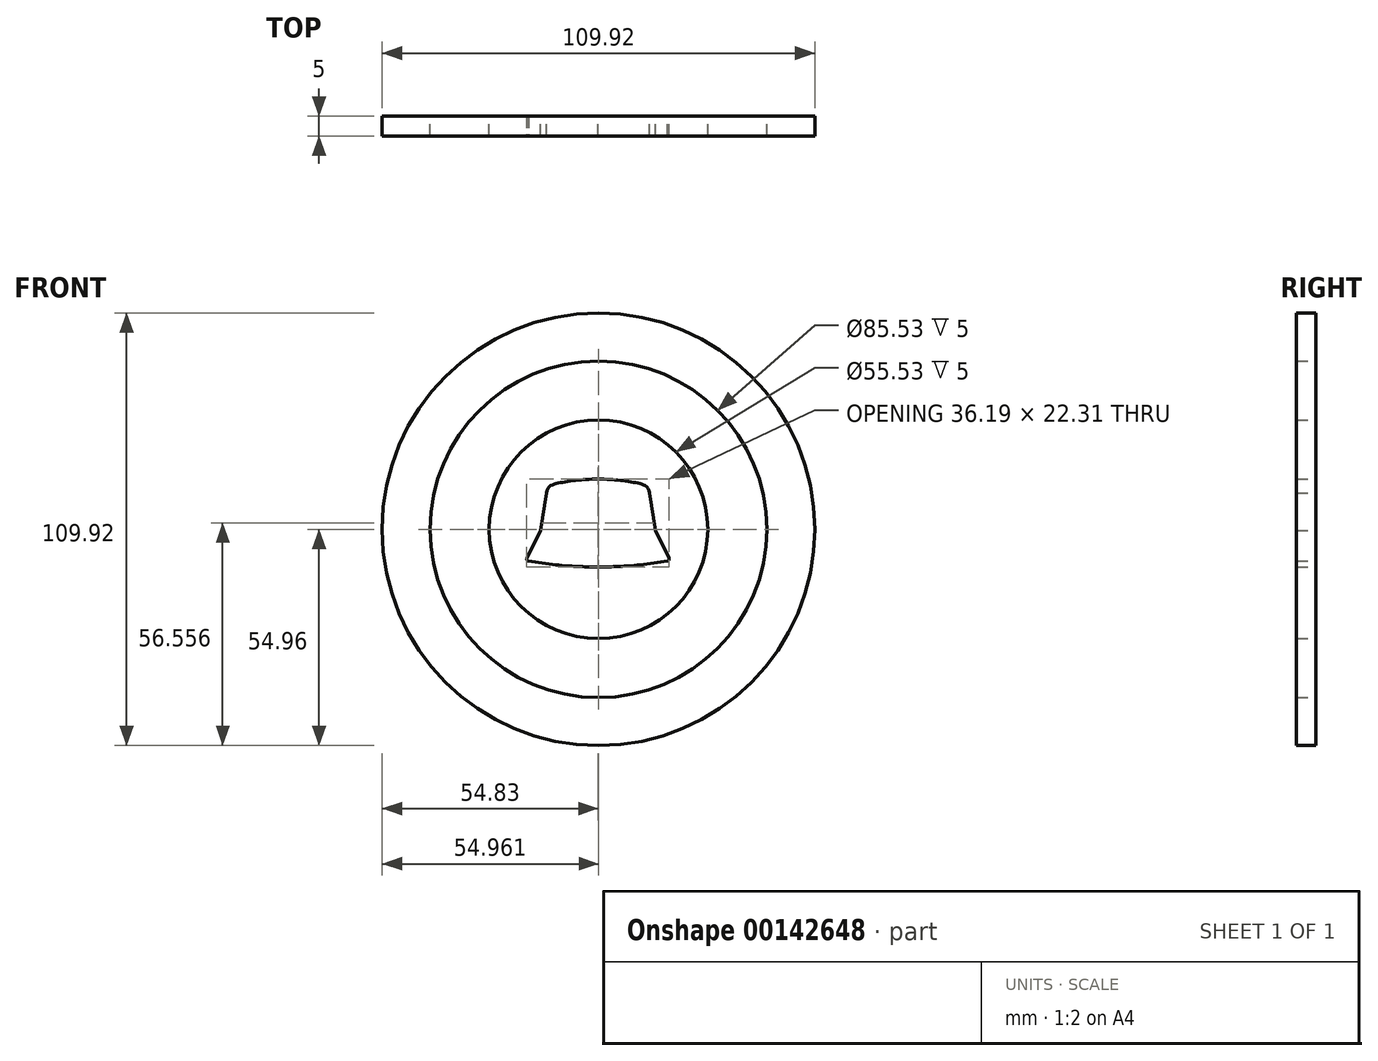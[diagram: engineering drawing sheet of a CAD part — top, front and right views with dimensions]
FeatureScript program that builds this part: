
annotation { "Feature Type Name" : "Feature", "Feature Type Description" : "" }
export const myFeature = defineFeature(function(context is Context, id is Id, definition is map)
    precondition{}
    {
        {
            var Q0;
            Q0=qCreatedBy(makeId("Front.planeOp"),FACE);
            var sketch = newSketch(context, id + "F0", { "sketchPlane" : qUnion([Q0])});
            skFitSpline(sketch, "E0", {"points": [v(0, 12.75) * mm, v(-4.84, 12.52) * mm, v(-9.06, 11.94) * mm, v(-11.63, 11.28) * mm, v(-13.13, 9.28) * mm], "startDerivative": vector(-19.15, 0) * mm, "endDerivative": vector(-1.8, -16.13) * mm});
            skLineSegment(sketch, "E1", {"start": v(-13.13, 9.28) * mm, "end": v(-14.61, -0.34) * mm});
            skLineSegment(sketch, "E2", {"start": v(-14.61, -0.34) * mm, "end": v(-18.03, -7.3) * mm});
            skFitSpline(sketch, "E3", {"points": [v(0, -9.56) * mm, v(-8.5, -9.24) * mm, v(-21.18, -7.47) * mm], "startDerivative": vector(-18.04, 0.14) * mm, "endDerivative": vector(-21.23, 3.62) * mm});
            skFitSpline(sketch, "E4", {"points": [v(-18.03, -7.3) * mm, v(-18.07, -7.75) * mm, v(-17.66, -8.05) * mm], "startDerivative": vector(-0.52, -1.06) * mm, "endDerivative": vector(1.76, -0.31) * mm});
            skFitSpline(sketch, "E5.MirrorCS", {"points": [v(0, 12.75) * mm, v(4.84, 12.52) * mm, v(9.06, 11.94) * mm, v(11.63, 11.28) * mm, v(13.13, 9.28) * mm], "startDerivative": vector(19.15, 0) * mm, "endDerivative": vector(1.8, -16.13) * mm});
            skLineSegment(sketch, "E6.MirrorCS", {"start": v(13.13, 9.28) * mm, "end": v(14.61, -0.34) * mm});
            skLineSegment(sketch, "E7.MirrorCS", {"start": v(14.61, -0.34) * mm, "end": v(18.03, -7.3) * mm});
            skFitSpline(sketch, "E8.MirrorCS", {"points": [v(0, -9.56) * mm, v(8.5, -9.24) * mm, v(21.18, -7.47) * mm], "startDerivative": vector(18.04, 0.14) * mm, "endDerivative": vector(21.23, 3.62) * mm});
            skFitSpline(sketch, "E9.MirrorCS", {"points": [v(18.03, -7.3) * mm, v(18.07, -7.75) * mm, v(17.66, -8.05) * mm], "startDerivative": vector(0.52, -1.06) * mm, "endDerivative": vector(-1.76, -0.31) * mm});
            skCircle(sketch, "E10", {"center": v(0.13, 0) * mm, "radius": 27.76 * mm});
            skLineSegment(sketch, "E11", {"start": v(0, 27.76) * mm, "end": v(24.6, 27.76) * mm, "construction": true});
            skLineSegment(sketch, "E12", {"start": v(27.9, 6.53) * mm, "end": v(27.9, -3.98) * mm, "construction": true});
            skCircle(sketch, "E13.0", {"center": v(0.13, 0) * mm, "radius": 42.76 * mm});
            skCircle(sketch, "E14.0", {"center": v(0.13, 0) * mm, "radius": 54.96 * mm});
            skLineSegment(sketch, "E15", {"start": v(-9.87, -27.76) * mm, "end": v(13.71, -27.76) * mm, "construction": true});
            skSolve(sketch);
        }
        {
            var Q0;
            Q0=makeQuery(id+"F0.imprint","IMPRINT",FACE,{"disambiguationData":[TD([[makeQuery(id+"F0.imprint","IMPRINT",EDGE,{"derivedFrom":sQuery(id+"F0.wireOp",EDGE,"E0")}),1.0]])]});
            extrude(context, id + "F1", {"entities" : qUnion([Q0]), "depth" : 5 * mm});
        }
        {
            var Q0;
            Q0=makeQuery(id+"F0.imprint","IMPRINT",FACE,{"disambiguationData":[TD([[makeQuery(id+"F0.imprint","IMPRINT",EDGE,{"derivedFrom":sQuery(id+"F0.wireOp",EDGE,"E0")}),-1.0]])]});
            extrude(context, id + "F2", {"entities" : qUnion([Q0]), "depth" : 5 * mm});
        }
        {
            var Q0;
            Q0=makeQuery(id+"F0.imprint","IMPRINT",FACE,{"disambiguationData":[TD([[makeQuery(id+"F0.imprint","IMPRINT",EDGE,{"derivedFrom":sQuery(id+"F0.wireOp",EDGE,"E10")}),-1.0]])]});
            extrude(context, id + "F3", {"entities" : qUnion([Q0]), "depth" : 5 * mm});
        }
        {
            var Q0;
            Q0=makeQuery(id+"F0.imprint","IMPRINT",FACE,{"disambiguationData":[TD([[makeQuery(id+"F0.imprint","IMPRINT",EDGE,{"derivedFrom":sQuery(id+"F0.wireOp",EDGE,"E13.0")}),-1.0]])]});
            extrude(context, id + "F4", {"entities" : qUnion([Q0]), "depth" : 5 * mm});
        }
    });
